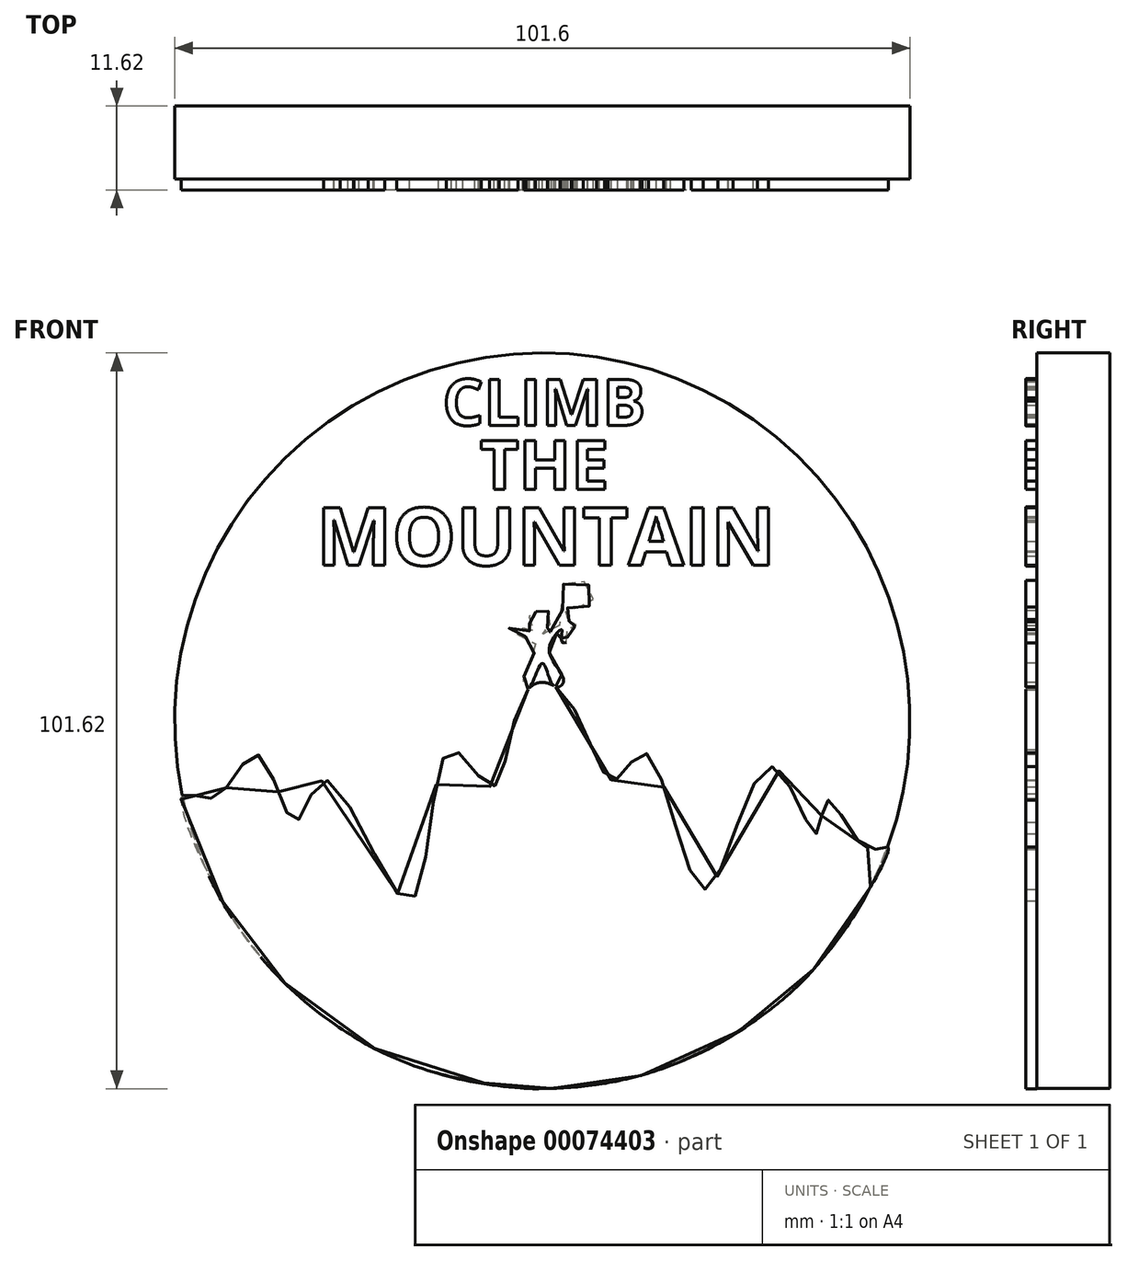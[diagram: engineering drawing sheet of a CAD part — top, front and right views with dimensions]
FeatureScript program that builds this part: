
annotation { "Feature Type Name" : "Feature", "Feature Type Description" : "" }
export const myFeature = defineFeature(function(context is Context, id is Id, definition is map)
    precondition{}
    {
        {
            var Q0;
            Q0=qCreatedBy(makeId("Front.planeOp"),FACE);
            var sketch = newSketch(context, id + "F0", { "sketchPlane" : qUnion([Q0])});
            skCircle(sketch, "E0", {"center": v(0, 0) * mm, "radius": 50.8 * mm});
            skSolve(sketch);
        }
        {
            var Q0;
            Q0=makeQuery(id+"F0.imprint","IMPRINT",FACE,{"disambiguationData":[TD([[makeQuery(id+"F0.imprint","IMPRINT",EDGE,{"derivedFrom":sQuery(id+"F0.wireOp",EDGE,"E0")}),1.0]])]});
            extrude(context, id + "F1", {"entities" : qUnion([Q0]), "depth" : 10.1 * mm});
        }
        {
            var Q0;
            Q0=makeQuery(id+"F1.opExtrude","CAP_FACE",FACE,{"disambiguationData":[OSD([sQuery(id+"F0.wireOp",EDGE,"E0")])],"isStart":false});
            var sketch = newSketch(context, id + "F2", { "sketchPlane" : qUnion([Q0])});
            skFitSpline(sketch, "E1", {"points": [v(-49.75, -10.3) * mm, v(-46.05, -21.44) * mm, v(-38.92, -32.65) * mm, v(-28.65, -41.95) * mm, v(-15.2, -48.47) * mm, v(-3.06, -50.7) * mm, v(0, -50.8) * mm, v(7.8, -50.2) * mm, v(18.91, -47.15) * mm, v(30.92, -40.3) * mm, v(38.44, -33.22) * mm, v(45.16, -23.27) * mm, v(47.7, -17.46) * mm, v(44.7, -17.47) * mm, v(39.37, -10.98) * mm, v(37.75, -15.62) * mm, v(31.48, -6.34) * mm, v(22.44, -23.27) * mm, v(14.32, -4.48) * mm, v(9.91, -8.2) * mm, v(3.42, 3.17) * mm, v(-2.38, 3.87) * mm, v(-7.02, -9.12) * mm, v(-12.82, -4.02) * mm, v(-18.38, -24.9) * mm, v(-29.98, -8.2) * mm, v(-34.15, -14) * mm, v(-39.26, -4.71) * mm, v(-44.13, -9.82) * mm, v(-47.37, -10.51) * mm, v(-49.75, -10.3) * mm]});
            skSolve(sketch);
        }
        {
            var Q0;
            Q0 = qSketchRegion(id + "F2", true);
            extrude(context, id + "F3", {"entities" : qUnion([Q0]), "operationType" : NewBodyOperationType.ADD, "depth" : 1.52 * mm});
        }
        {
            var Q0;
            Q0=makeQuery(id+"F3.boolean.opBoolean","SPLIT",FACE,{"disambiguationData":[OD(0.0)],"derivedFrom":makeQuery(id+"F1.opExtrude","CAP_FACE",FACE,{"disambiguationData":[OSD([sQuery(id+"F0.wireOp",EDGE,"E0")])],"isStart":false})});
            var sketch = newSketch(context, id + "F4", { "sketchPlane" : qUnion([Q0])});
            skFitSpline(sketch, "E2", {"points": [v(-1.75, 7.82) * mm, v(-2.68, 5.02) * mm, v(-2, 4.35) * mm, v(0, 7.94) * mm, v(1.6, 4.84) * mm, v(2.91, 5.26) * mm, v(1.28, 8.64) * mm, v(1.28, 11.08) * mm, v(2.68, 12.6) * mm, v(2.68, 10.97) * mm, v(3.5, 10.97) * mm, v(3.5, 12.71) * mm, v(4.66, 13.18) * mm, v(3.96, 14) * mm, v(3.5, 13.65) * mm, v(3.5, 15.63) * mm, v(6.53, 15.86) * mm, v(6.3, 18.9) * mm, v(2.56, 18.43) * mm, v(2.68, 13.65) * mm, v(0, 12.02) * mm, v(1.17, 13.53) * mm, v(0.82, 15.16) * mm, v(0, 15.16) * mm, v(-1.28, 14.93) * mm, v(-1.86, 13.65) * mm, v(-1.17, 12.13) * mm, v(-3.96, 13.18) * mm, v(-4.55, 12.25) * mm, v(-1.28, 11.2) * mm, v(-1.75, 7.82) * mm]});
            skSolve(sketch);
        }
        {
            var Q0;
            Q0 = qSketchRegion(id + "F4", true);
            extrude(context, id + "F5", {"entities" : qUnion([Q0]), "operationType" : NewBodyOperationType.ADD, "depth" : 1.52 * mm});
        }
        {
            var Q0;
            {var subQ0=sQuery(id+"F0.wireOp",EDGE,"E0");var subQ1=sQuery(id+"F2.wireOp",EDGE,"E1");Q0=makeQuery(id+"F5.boolean.opBoolean","SPLIT",FACE,{"disambiguationData":[TD([makeQuery(id+"F1.opExtrude","SWEPT_FACE",FACE,{"disambiguationData":[OSD([subQ0])]}),makeQuery(id+"F3.opExtrude","SWEPT_FACE",FACE,{"disambiguationData":[OSD([subQ1])]}),makeQuery(id+"F3.opExtrude","CAP_FACE",FACE,{"disambiguationData":[OSD([subQ1])],"isStart":true}),makeQuery(id+"F5.opExtrude","SWEPT_FACE",FACE,{"disambiguationData":[OSD([sQuery(id+"F4.wireOp",EDGE,"E2")])]})])],"derivedFrom":makeQuery(id+"F3.boolean.opBoolean","SPLIT",FACE,{"disambiguationData":[OD(0.0)],"derivedFrom":makeQuery(id+"F1.opExtrude","CAP_FACE",FACE,{"disambiguationData":[OSD([subQ0])],"isStart":false})})});}
            var sketch = newSketch(context, id + "F6", { "sketchPlane" : qUnion([Q0])});
            skText(sketch, "E3", { "text": "CLIMB", "fontName": "OpenSans-Bold.ttf"});
            skText(sketch, "E4", { "text": "THE\n", "fontName": "OpenSans-Bold.ttf"});
            skText(sketch, "E5", { "text": "MOUNTAIN\n", "fontName": "OpenSans-Bold.ttf"});
            const initialGuessF6  = {"E3": [-0.01378, 0.04081, 1, 0, 0.00641], "E4": [-0.00866, 0.03196, 1, 0, 0.00676], "E5": [-0.03123, 0.02147, 1, 0, 0.00799]};
            skSetInitialGuess(sketch, initialGuessF6);
            skSolve(sketch);
        }
        {
            var Q0;
            Q0 = qSketchRegion(id + "F6", true);
            extrude(context, id + "F7", {"entities" : qUnion([Q0]), "operationType" : NewBodyOperationType.ADD, "depth" : 1.52 * mm});
        }
        {
            var Q0;
            Q0=makeQuery(id+"F0.imprint","IMPRINT",FACE,{"disambiguationData":[TD([[makeQuery(id+"F0.imprint","IMPRINT",EDGE,{"derivedFrom":sQuery(id+"F0.wireOp",EDGE,"E0")}),1.0]])]});
            var sketch = newSketch(context, id + "F8", { "sketchPlane" : qUnion([Q0])});
            skText(sketch, "E6", { "text": "Myla", "fontName": "OpenSans-Regular.ttf"});
            const initialGuessF8  = {"E6": [-0.00899, -0.04474, 1, 0, 0.00606]};
            skSetInitialGuess(sketch, initialGuessF8);
            skSolve(sketch);
        }
        {
            var Q0;
            Q0 = qSketchRegion(id + "F8", true);
            extrude(context, id + "F9", {"entities" : qUnion([Q0]), "operationType" : NewBodyOperationType.ADD, "depth" : 4.7 * mm});
        }
        {
            var Q0;
            Q0=makeQuery(id+"F1.opExtrude","SWEPT_BODY",BODY,{"disambiguationData":[OSD([sQuery(id+"F0.wireOp",EDGE,"E0")])]});
            transform(context, id + "F10", {"entities" : qUnion([Q0]), "transformType" : TransformType.TRANSLATION_3D, "dx" : 1.95 * mm, "dy" : 11.2 * mm, "dz" : -45.26 * mm, "makeCopy" : false});
        }
    });
